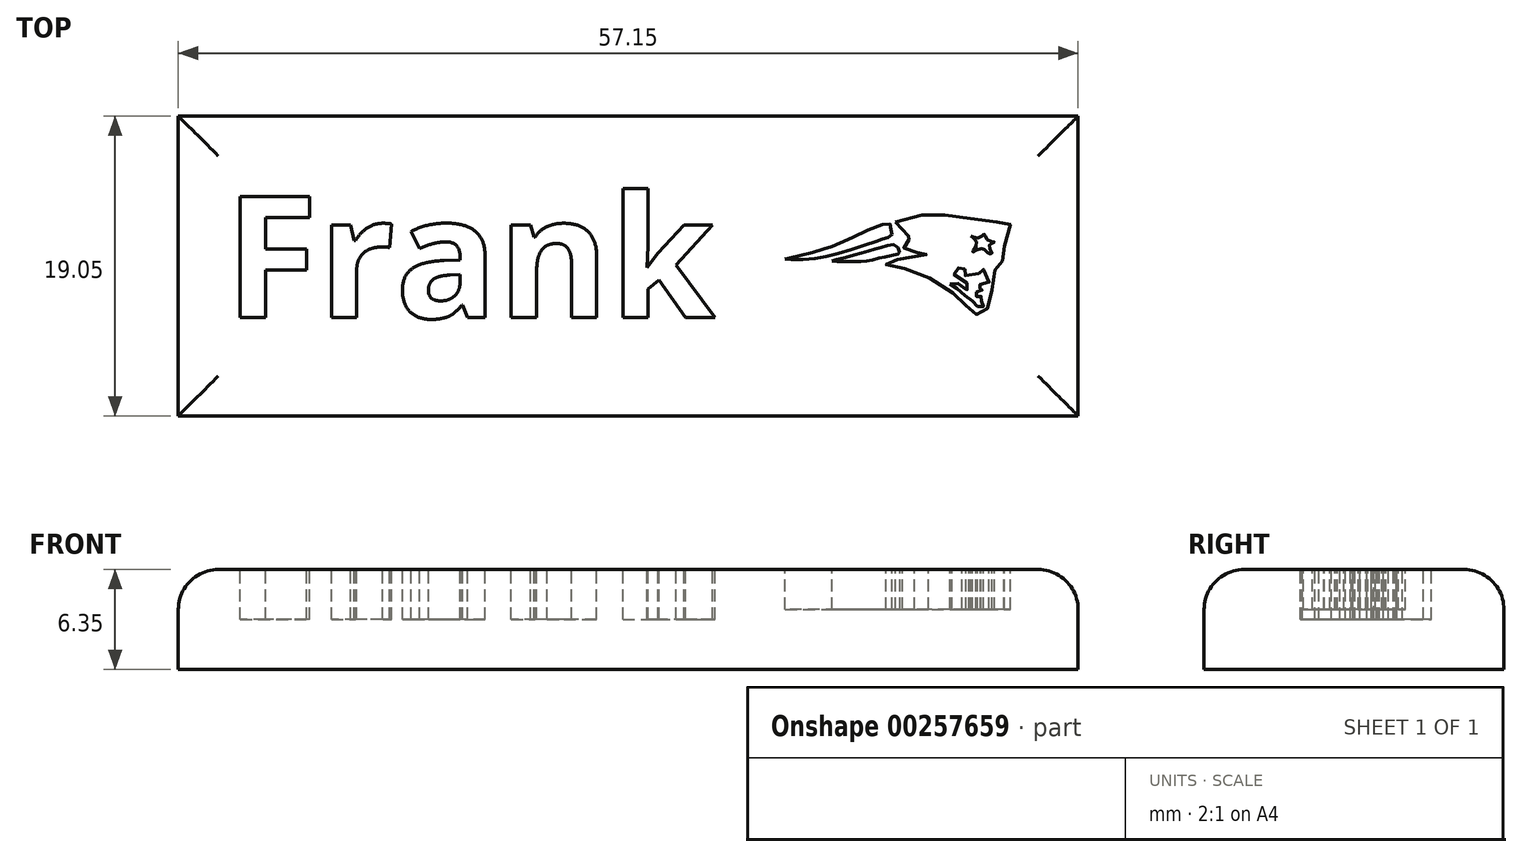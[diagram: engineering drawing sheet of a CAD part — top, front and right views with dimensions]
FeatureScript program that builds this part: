
annotation { "Feature Type Name" : "Feature", "Feature Type Description" : "" }
export const myFeature = defineFeature(function(context is Context, id is Id, definition is map)
    precondition{}
    {
        {
            var Q0;
            Q0=qCreatedBy(makeId("Top.planeOp"),FACE);
            var sketch = newSketch(context, id + "F0", { "sketchPlane" : qUnion([Q0])});
            skLineSegment(sketch, "E0.bottom", {"start": v(-45.56, -2.16) * mm, "end": v(11.6, -2.16) * mm});
            skLineSegment(sketch, "E0.top", {"start": v(-45.56, -21.2) * mm, "end": v(11.6, -21.2) * mm});
            skLineSegment(sketch, "E0.left", {"start": v(-45.56, -2.16) * mm, "end": v(-45.56, -21.2) * mm});
            skLineSegment(sketch, "E0.right", {"start": v(11.6, -2.16) * mm, "end": v(11.6, -21.2) * mm});
            skSolve(sketch);
        }
        {
            var Q0;
            Q0=makeQuery(id+"F0.imprint","IMPRINT",FACE,{"disambiguationData":[TD([[makeQuery(id+"F0.imprint","IMPRINT",EDGE,{"derivedFrom":sQuery(id+"F0.wireOp",EDGE,"E0.bottom")}),-1.0]])]});
            extrude(context, id + "F1", {"entities" : qUnion([Q0]), "depth" : 6.35 * mm});
        }
        {
            var Q0;
            Q0=makeQuery(id+"F1.opExtrude","CAP_FACE",FACE,{"disambiguationData":[OSD([sQuery(id+"F0.wireOp",EDGE,"E0.bottom"),sQuery(id+"F0.wireOp",EDGE,"E0.top"),sQuery(id+"F0.wireOp",EDGE,"E0.left"),sQuery(id+"F0.wireOp",EDGE,"E0.right")])],"isStart":false});
            var sketch = newSketch(context, id + "F2", { "sketchPlane" : qUnion([Q0])});
            skText(sketch, "E1", { "text": "Frank", "fontName": "OpenSans-Bold.ttf"});
            const initialGuessF2  = {"E1": [-0.0426, -0.01497, 1, 0, 0.00777]};
            skSetInitialGuess(sketch, initialGuessF2);
            skSolve(sketch);
        }
        {
            var Q0;
            Q0 = qSketchRegion(id + "F2", true);
            extrude(context, id + "F3", {"entities" : qUnion([Q0]), "operationType" : NewBodyOperationType.REMOVE, "oppositeDirection" : true, "depth" : 3.17 * mm});
        }
        {
            var Q0;
            Q0=makeQuery(id+"F1.opExtrude","CAP_EDGE",EDGE,{"disambiguationData":[OSD([sQuery(id+"F0.wireOp",EDGE,"E0.bottom")])],"isStart":false});
            var Q1;
            Q1=makeQuery(id+"F1.opExtrude","CAP_EDGE",EDGE,{"disambiguationData":[OSD([sQuery(id+"F0.wireOp",EDGE,"E0.right")])],"isStart":false});
            var Q2;
            Q2=makeQuery(id+"F1.opExtrude","CAP_EDGE",EDGE,{"disambiguationData":[OSD([sQuery(id+"F0.wireOp",EDGE,"E0.top")])],"isStart":false});
            var Q3;
            Q3=makeQuery(id+"F1.opExtrude","CAP_EDGE",EDGE,{"disambiguationData":[OSD([sQuery(id+"F0.wireOp",EDGE,"E0.left")])],"isStart":false});
            fillet(context, id + "F4", {"entities" : qUnion([Q0, Q1, Q2, Q3]), "radius" : 2.54 * mm, "tangentPropagation" : true, "allowEdgeOverflow" : false});
        }
        {
            var Q0;
            {var subQ0=sQuery(id+"F0.wireOp",EDGE,"E0.top");var subQ1=sQuery(id+"F0.wireOp",EDGE,"E0.right");var subQ2=sQuery(id+"F0.wireOp",EDGE,"E0.bottom");var subQ3=sQuery(id+"F0.wireOp",EDGE,"E0.left");Q0=makeQuery(id+"F3.boolean.opBoolean","SPLIT",FACE,{"disambiguationData":[TD([makeQuery(id+"F1.opExtrude","SWEPT_FACE",FACE,{"disambiguationData":[OSD([subQ2])]})])],"derivedFrom":makeQuery(id+"F1.opExtrude","CAP_FACE",FACE,{"disambiguationData":[OSD([subQ2,subQ0,subQ3,subQ1])],"isStart":false})});}
            var sketch = newSketch(context, id + "F5", { "sketchPlane" : qUnion([Q0])});
            skSolve(sketch);
        }
        {
            var Q0;
            {var subQ27=sQuery(id+"F2.wireOp",EDGE,"E1.sketch_text.stroke-0");Q0=makeQuery(id+"F5.imprint","IMPRINT",FACE,{"disambiguationData":[TD([[makeQuery(id+"F5.imprint","IMPRINT",EDGE,{"derivedFrom":makeQuery(id+"F3.boolean.opBoolean","COPY",EDGE,{"derivedFrom":makeQuery(id+"F3.opExtrude","CAP_EDGE",EDGE,{"disambiguationData":[OSD([subQ27])],"isStart":true})})}),1.0]])]});}
            var sketch = newSketch(context, id + "F6", { "sketchPlane" : qUnion([Q0])});
            skFitSpline(sketch, "E2", {"points": [v(-7.01, -11.23) * mm, v(-6.43, -11.11) * mm, v(-4.4, -10.55) * mm, v(-3.23, -10.1) * mm, v(-0.4, -9) * mm, v(-0.29, -9.34) * mm, v(-0.24, -9.73) * mm, v(-0.65, -9.92) * mm, v(-1.23, -10.12) * mm, v(-3.71, -10.92) * mm, v(-5.7, -11.26) * mm, v(-7.01, -11.23) * mm]});
            skFitSpline(sketch, "E3", {"points": [v(-4.03, -11.36) * mm, v(-3.27, -11.16) * mm, v(-2.1, -10.85) * mm, v(-1.3, -10.6) * mm, v(-0.58, -10.4) * mm, v(0, -10.36) * mm, v(0.25, -10.75) * mm, v(0.25, -10.87) * mm, v(-0.31, -11.04) * mm, v(-1.04, -11.19) * mm, v(-1.72, -11.36) * mm, v(-2.3, -11.4) * mm, v(-2.79, -11.4) * mm, v(-3.37, -11.4) * mm, v(-4.03, -11.36) * mm]});
            skFitSpline(sketch, "E4", {"points": [v(0, -8.88) * mm, v(1.49, -8.47) * mm, v(2.63, -8.42) * mm, v(4.04, -8.54) * mm, v(5.42, -8.78) * mm, v(6.76, -8.88) * mm, v(7.1, -8.88) * mm, v(7.3, -9.15) * mm, v(6.93, -10.29) * mm, v(6.9, -10.7) * mm, v(6.8, -11.26) * mm, v(6.7, -11.65) * mm, v(6.49, -11.84) * mm, v(6.25, -12.04) * mm, v(6.15, -13.13) * mm, v(6.05, -13.35) * mm, v(5.83, -14.4) * mm, v(5.35, -14.9) * mm, v(5.13, -14.76) * mm, v(4.86, -14.46) * mm, v(4.55, -14.27) * mm, v(4.08, -13.8) * mm, v(3.55, -13.32) * mm, v(2.04, -12.4) * mm, v(0.7, -11.87) * mm, v(-0.58, -11.72) * mm, v(-0.6, -11.6) * mm, v(-0.48, -11.5) * mm, v(-0.31, -11.4) * mm, v(0.83, -11.14) * mm, v(2.1, -10.92) * mm, v(1.63, -10.87) * mm, v(1.17, -10.82) * mm, v(0.78, -10.9) * mm, v(0.44, -10.12) * mm, v(0.59, -10.02) * mm, v(0.85, -10) * mm, v(1.2, -9.87) * mm, v(0.95, -9.75) * mm, v(0.64, -9.78) * mm, v(0, -8.88) * mm]});
            skFitSpline(sketch, "E5", {"points": [v(4.79, -9.78) * mm, v(5.3, -9.9) * mm, v(5.64, -9.66) * mm, v(5.83, -10.02) * mm, v(6.27, -10.17) * mm, v(5.95, -10.36) * mm, v(6.12, -10.9) * mm, v(5.86, -10.85) * mm, v(5.47, -10.58) * mm, v(4.89, -10.8) * mm, v(5.15, -10.24) * mm, v(4.79, -9.78) * mm]});
            skFitSpline(sketch, "E6", {"points": [v(3.45, -12.81) * mm, v(3.91, -12.76) * mm, v(4.57, -13.2) * mm, v(4.57, -12.81) * mm, v(3.6, -12.04) * mm, v(4.45, -11.77) * mm, v(4.23, -12.16) * mm, v(5.25, -12.18) * mm, v(5.52, -11.84) * mm, v(5.9, -12.81) * mm, v(5.2, -12.89) * mm, v(5.37, -13.13) * mm, v(5.57, -13.23) * mm, v(5.42, -13.23) * mm, v(5.15, -13.32) * mm, v(5.15, -13.42) * mm, v(5.1, -13.59) * mm, v(5.3, -13.59) * mm, v(5.42, -13.59) * mm, v(5.4, -13.74) * mm, v(5.44, -13.88) * mm, v(5.54, -14.1) * mm, v(5.54, -14.32) * mm, v(5.2, -14.25) * mm, v(4.93, -13.95) * mm, v(4.5, -13.64) * mm, v(3.87, -13.08) * mm, v(3.45, -12.81) * mm]});
            skSolve(sketch);
        }
        {
            var Q0;
            Q0 = qSketchRegion(id + "F6", true);
            extrude(context, id + "F7", {"entities" : qUnion([Q0]), "operationType" : NewBodyOperationType.REMOVE, "oppositeDirection" : true, "depth" : 2.54 * mm});
        }
    });
